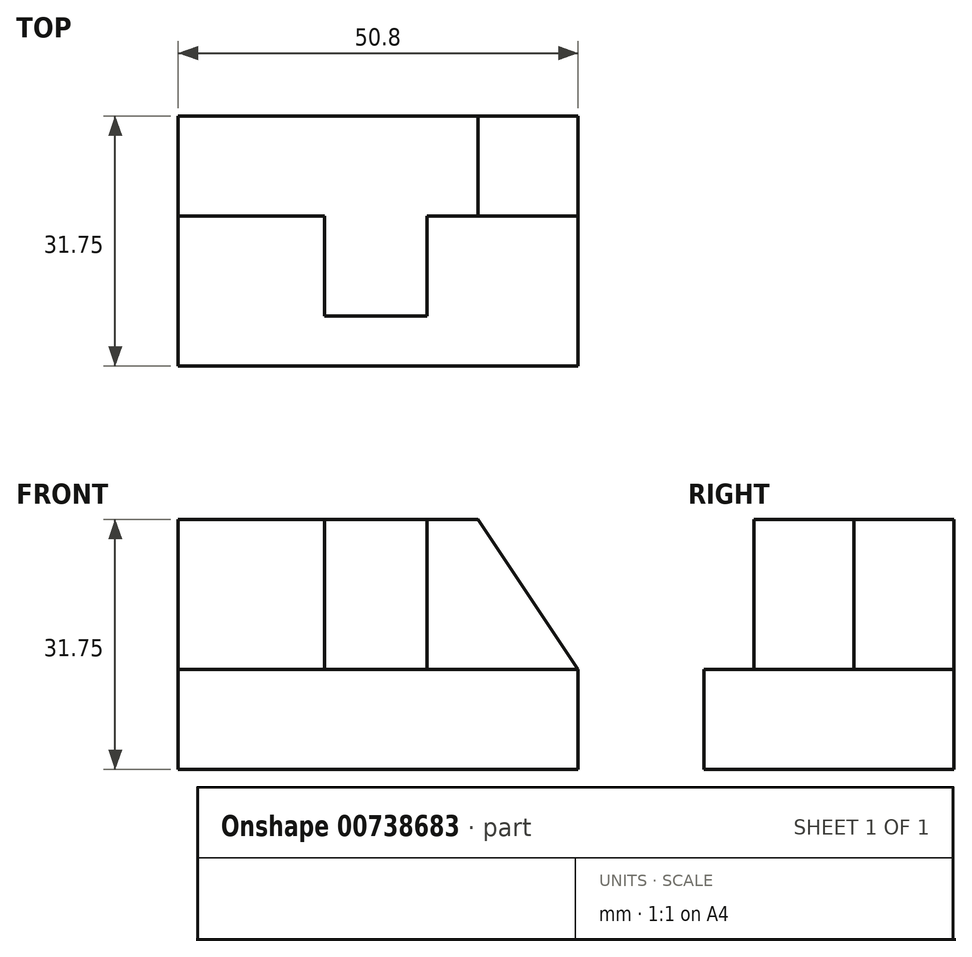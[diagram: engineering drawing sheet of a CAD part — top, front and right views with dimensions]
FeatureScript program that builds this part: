
annotation { "Feature Type Name" : "Feature", "Feature Type Description" : "" }
export const myFeature = defineFeature(function(context is Context, id is Id, definition is map)
    precondition{}
    {
        {
            var Q0;
            Q0=qCreatedBy(makeId("Front.planeOp"),FACE);
            var sketch = newSketch(context, id + "F0", { "sketchPlane" : qUnion([Q0])});
            skLineSegment(sketch, "E0", {"start": v(0, 0) * mm, "end": v(50.8, 0) * mm});
            skLineSegment(sketch, "E1", {"start": v(50.8, 0) * mm, "end": v(50.8, 31.75) * mm});
            skLineSegment(sketch, "E2", {"start": v(50.8, 31.75) * mm, "end": v(0, 31.75) * mm});
            skLineSegment(sketch, "E3", {"start": v(0, 31.75) * mm, "end": v(0, 0) * mm});
            skSolve(sketch);
        }
        {
            var Q0;
            Q0=makeQuery(id+"F0.imprint","IMPRINT",FACE,{"disambiguationData":[TD([[makeQuery(id+"F0.imprint","IMPRINT",EDGE,{"derivedFrom":sQuery(id+"F0.wireOp",EDGE,"E0")}),1.0]])]});
            extrude(context, id + "F1", {"entities" : qUnion([Q0]), "depth" : 31.75 * mm, "offsetDistance" : 25.4 * mm});
        }
        {
            var Q0;
            Q0=makeQuery(id+"F1.opExtrude","SWEPT_FACE",FACE,{"disambiguationData":[OSD([sQuery(id+"F0.wireOp",EDGE,"E1")])]});
            var sketch = newSketch(context, id + "F2", { "sketchPlane" : qUnion([Q0])});
            skLineSegment(sketch, "E4", {"start": v(-31.75, 0) * mm, "end": v(-31.75, 12.7) * mm});
            skLineSegment(sketch, "E5", {"start": v(-31.75, 12.7) * mm, "end": v(-12.7, 12.7) * mm});
            skLineSegment(sketch, "E6", {"start": v(-12.7, 12.7) * mm, "end": v(-12.7, 31.75) * mm});
            skSolve(sketch);
        }
        {
            var Q0;
            {var subQ0=sQuery(id+"F2.wireOp",EDGE,"E5");Q0=makeQuery(id+"F2.imprint","IMPRINT",FACE,{"disambiguationData":[TD([[makeQuery(id+"F2.imprint","IMPRINT",EDGE,{"derivedFrom":subQ0}),1.0]])]});}
            extrude(context, id + "F3", {"entities" : qUnion([Q0]), "operationType" : NewBodyOperationType.REMOVE, "oppositeDirection" : true, "depth" : 50.8 * mm, "offsetDistance" : 25.4 * mm});
        }
        {
            var Q0;
            Q0=makeQuery(id+"F3.boolean.opBoolean","COPY",FACE,{"derivedFrom":makeQuery(id+"F3.opExtrude","SWEPT_FACE",FACE,{"disambiguationData":[OSD([sQuery(id+"F2.wireOp",EDGE,"E6")])]})});
            var sketch = newSketch(context, id + "F4", { "sketchPlane" : qUnion([Q0])});
            skLineSegment(sketch, "E7", {"start": v(0, 31.75) * mm, "end": v(38.1, 31.75) * mm});
            skLineSegment(sketch, "E8", {"start": v(38.1, 31.75) * mm, "end": v(50.8, 12.7) * mm});
            skSolve(sketch);
        }
        {
            var Q0;
            {var subQ0=sQuery(id+"F4.wireOp",EDGE,"E8");Q0=makeQuery(id+"F4.imprint","IMPRINT",FACE,{"disambiguationData":[TD([[makeQuery(id+"F4.imprint","IMPRINT",EDGE,{"derivedFrom":subQ0}),1.0]])]});}
            extrude(context, id + "F5", {"entities" : qUnion([Q0]), "operationType" : NewBodyOperationType.REMOVE, "oppositeDirection" : true, "depth" : 25.4 * mm, "offsetDistance" : 25.4 * mm});
        }
        {
            var Q0;
            Q0=makeQuery(id+"F3.boolean.opBoolean","COPY",FACE,{"derivedFrom":makeQuery(id+"F3.opExtrude","SWEPT_FACE",FACE,{"disambiguationData":[OSD([sQuery(id+"F2.wireOp",EDGE,"E6")])]})});
            var sketch = newSketch(context, id + "F6", { "sketchPlane" : qUnion([Q0])});
            skLineSegment(sketch, "E9", {"start": v(31.64, 12.7) * mm, "end": v(31.64, 31.75) * mm});
            skLineSegment(sketch, "E10", {"start": v(18.58, 12.7) * mm, "end": v(18.58, 31.75) * mm});
            skSolve(sketch);
        }
        {
            var Q0;
            {var subQ0=sQuery(id+"F6.wireOp",EDGE,"E9");Q0=makeQuery(id+"F6.imprint","IMPRINT",FACE,{"disambiguationData":[TD([[makeQuery(id+"F6.imprint","IMPRINT",EDGE,{"derivedFrom":subQ0}),1.0]])]});}
            extrude(context, id + "F7", {"entities" : qUnion([Q0]), "operationType" : NewBodyOperationType.ADD, "depth" : 12.7 * mm, "offsetDistance" : 25.4 * mm});
        }
    });
